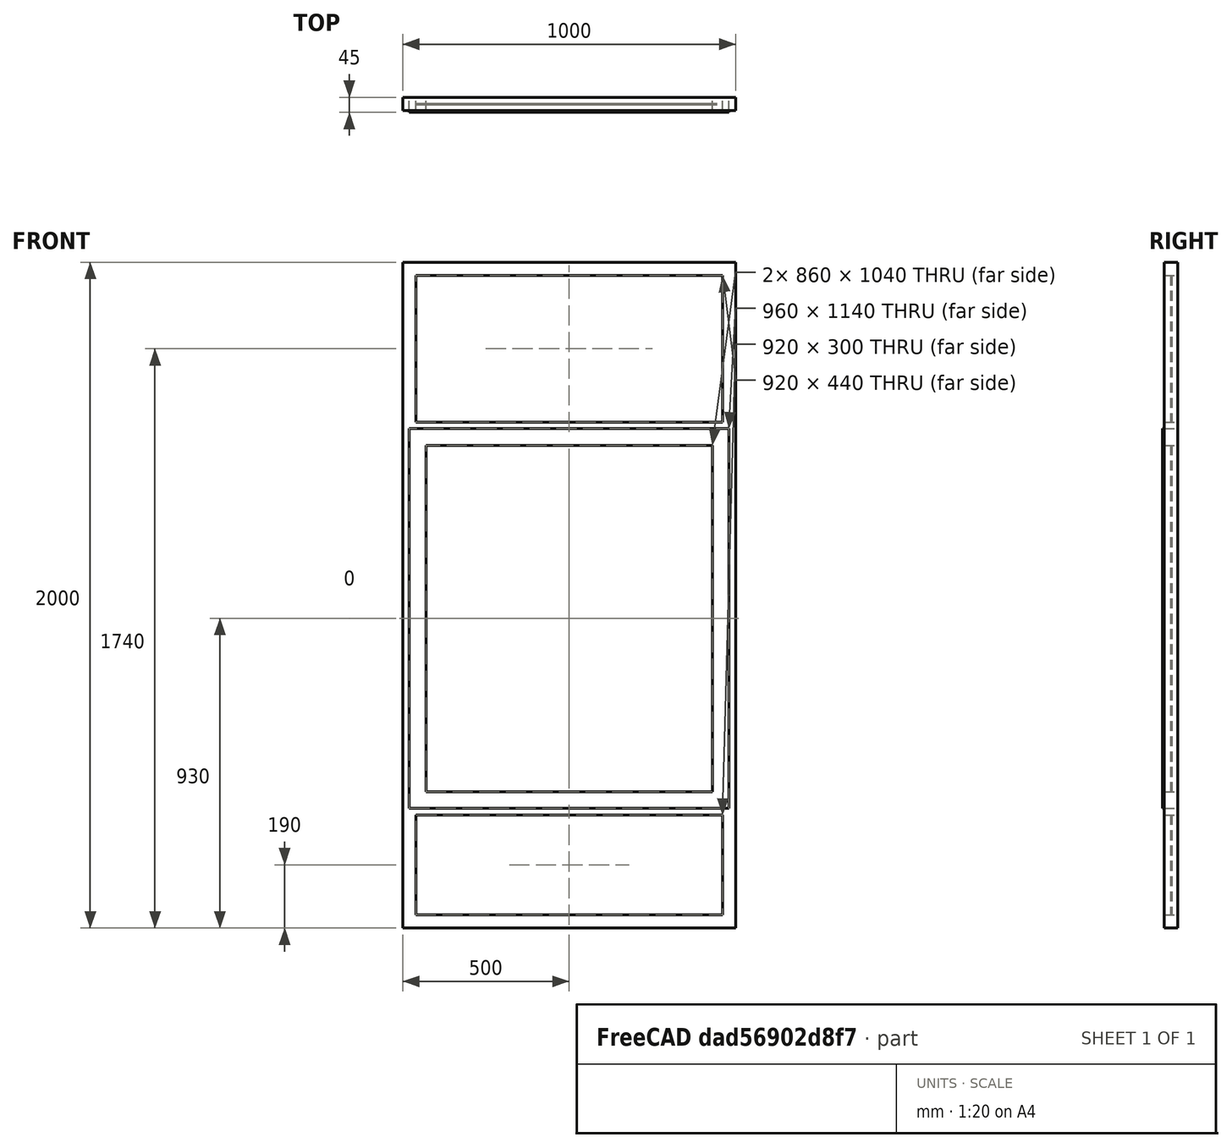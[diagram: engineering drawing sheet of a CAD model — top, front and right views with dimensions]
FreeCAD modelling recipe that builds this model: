
FCSTD DOCUMENT  (FreeCAD 0.16R6704 (Git))
Label: Maxim Air with fixed glass
License: CreativeCommons Attribution
LicenseURL: http://creativecommons.org/licenses/by/4.0/
objects: Sketcher::SketchObject×2, Part::FeaturePython×1, App::DocumentObjectGroup×1
note: 3 computed .brp shape members not serialized (recipe doc carries the construction recipe); baked Part::Feature solids carry a one-line shape summary decoded from their .brp

FEATURE [Sketcher::SketchObject] Sketch187
  Placement = pos=(0,0,0) rot=(1,0,0;1.5708rad)
  sketch-geometry (24):
    g0: LineSegment StartX=1000 StartY=2000 StartZ=0 EndX=0 EndY=2000 EndZ=0
    g1: LineSegment StartX=0 StartY=2000 StartZ=0 EndX=0 EndY=0 EndZ=0
    g2: LineSegment StartX=0 StartY=0 StartZ=0 EndX=1000 EndY=0 EndZ=0
    g3: LineSegment StartX=1000 StartY=0 StartZ=0 EndX=1000 EndY=2000 EndZ=0
    g4: LineSegment StartX=40 StartY=340 StartZ=0 EndX=960 EndY=340 EndZ=0
    g5: LineSegment StartX=960 StartY=340 StartZ=0 EndX=960 EndY=40 EndZ=0
    g6: LineSegment StartX=960 StartY=40 StartZ=0 EndX=40 EndY=40 EndZ=0
    g7: LineSegment StartX=40 StartY=40 StartZ=0 EndX=40 EndY=340 EndZ=0
    g8: LineSegment StartX=40 StartY=1960 StartZ=0 EndX=960 EndY=1960 EndZ=0
    g9: LineSegment StartX=960 StartY=1960 StartZ=0 EndX=960 EndY=1520 EndZ=0
    g10: LineSegment StartX=960 StartY=1520 StartZ=0 EndX=40 EndY=1520 EndZ=0
    g11: LineSegment StartX=40 StartY=1520 StartZ=0 EndX=40 EndY=1960 EndZ=0
    g12: LineSegment StartX=20 StartY=1500 StartZ=0 EndX=980 EndY=1500 EndZ=0
    g13: LineSegment StartX=980 StartY=1500 StartZ=0 EndX=980 EndY=360 EndZ=0
    g14: LineSegment StartX=980 StartY=360 StartZ=0 EndX=20 EndY=360 EndZ=0
    g15: LineSegment StartX=20 StartY=360 StartZ=0 EndX=20 EndY=1500 EndZ=0
    g16: LineSegment StartX=70 StartY=1450 StartZ=0 EndX=930 EndY=1450 EndZ=0
    g17: LineSegment StartX=930 StartY=1450 StartZ=0 EndX=930 EndY=410 EndZ=0
    g18: LineSegment StartX=930 StartY=410 StartZ=0 EndX=70 EndY=410 EndZ=0
    g19: LineSegment StartX=70 StartY=410 StartZ=0 EndX=70 EndY=1450 EndZ=0
    g20: LineSegment StartX=40 StartY=380 StartZ=0 EndX=960 EndY=380 EndZ=0
    g21: LineSegment StartX=960 StartY=380 StartZ=0 EndX=960 EndY=1480 EndZ=0
    g22: LineSegment StartX=960 StartY=1480 StartZ=0 EndX=40 EndY=1480 EndZ=0
    g23: LineSegment StartX=40 StartY=1480 StartZ=0 EndX=40 EndY=380 EndZ=0
  constraints (71):
    c: Coincident(g0,g1)
    c: Horizontal(g0)
    c: Coincident(g1,g2)
    c: Vertical(g1)
    c: Coincident(g2,g3)
    c: Horizontal(g2)
    c: Coincident(g3,g0)
    c: Coincident(g4,g5)
    c: Horizontal(g4)
    c: Coincident(g5,g6)
    c: Vertical(g5)
    c: Coincident(g6,g7)
    c: Horizontal(g6)
    c: Coincident(g7,g4)
    c: Coincident(g8,g9)
    c: Horizontal(g8)
    c: Coincident(g9,g10)
    c: Vertical(g9)
    c: Coincident(g10,g11)
    c: Horizontal(g10)
    c: Coincident(g11,g8)
    c: Coincident(g12,g13)
    c: Horizontal(g12)
    c: Coincident(g13,g14)
    c: Vertical(g13)
    c: Coincident(g14,g15)
    c: Horizontal(g14)
    c: Coincident(g15,g12)
    c: Coincident(g16,g17)
    c: Horizontal(g16)
    c: Coincident(g17,g18)
    c: Vertical(g17)
    c: Coincident(g18,g19)
    c: Horizontal(g18)
    c: Coincident(g19,g16)
    c: Coincident(g20,g21)
    c: Horizontal(g20)
    c: Coincident(g21,g22)
    c: Vertical(g21)
    c: Coincident(g22,g23)
    c: Horizontal(g22)
    c: Coincident(g23,g20)
    c: DistanceX(g-1,g2) = 1000  'Largura do vão'
    c: DistanceY(g-1,g0) = 2000  'Altura do vão'
    c: Coincident(g1,g-1)
    c: DistanceX(g-1,g6) = 40  'Largura perfil vertical 1'
    c: DistanceY(g-1,g6) = 40  'Altura perfil inferior'
    c: DistanceY(g6,g4) = 300  'Altura vidro inferior'
    c: DistanceX(g20,g4) = 0  'Constraint49'
    c: DistanceX(g20,g4) = 0
    c: DistanceX(g10,g22) = 0
    c: DistanceX(g9,g21) = 0
    c: DistanceY(g8,g0) = 40  'Altura perfil superior'
    c: DistanceX(g5,g2) = 40  'Largura perfil vertical 2'
    c: DistanceY(g22,g10) = 40  'Altura perfil bandeira'
    c: DistanceY(g4,g20) = 40  'Altura montantel inferior maximar'
    c: DistanceX(g22,g16) = 30  'Largura perfil vertical 1 maximar'
    c: DistanceY(g16,g22) = 30  'Aaltura perfil superior maximar'
    c: DistanceX(g16,g21) = 30  'Largura perfil vertical 2 maximar'
    c: Vertical(g11)
    c: Vertical(g23)
    c: DistanceY(g20,g18) = 30  'Altura perfil inferior maximar'
    c: DistanceY(g22,g12) = 20  'Altura arremate superior'
    c: DistanceX(g12,g22) = 20  'Largura arremate vertical 1'
    c: DistanceX(g21,g12) = 20  'Largura arremate vertical 2'
    c: DistanceY(g14,g20) = 20  'Altura arremate inferior'
    c: Vertical(g7)
    c: Vertical(g19)
    c: Vertical(g15)
    c: DistanceY(g20,g22) = 1100  'Altura maximar'
    c: Vertical(g3)
FEATURE [Part::FeaturePython] Window118  label="Maxim Air with fixed glass "  # WARN: FeaturePython — macro-defined, semantics opaque (R4)
  Base = -> Sketch187
  Height = 0
  HoleDepth = 0
  MoveWithHost = true
  Normal = (0,1,0)
  Preset = 0
  Role = 0
  Width = 0
  WindowParts = CAIXILHO | Frame | Wire0,Wire1,Wire2,Wire3 | 40.0 | 0.0 | JANELA | Frame | Wire3,Wire4 | 40.0 | 0.0 | ARREMATE | Frame | Wire4,Wire3 | 5.0 | -5.0 | VIDRO SUPERIOR | Glass panel | Wire2 | 4.0 | 18.0 | VIDRO MAXIMAR | Glass panel | Wire4 | 4.0 | 18.0 | VIDRO INFERIOR | Glass panel | Wire1 | 4.0 | 18.0
FEATURE [Sketcher::SketchObject] Sketch188  label="Opening indication "
  ExternalGeometry = -> [Window118]
  Placement = pos=(0,18,0) rot=(1,0,0;1.5708rad)
  Support = -> Window118 [Face49]
  sketch-geometry (3):
    g0: LineSegment [constr] StartX=500 StartY=2100 StartZ=0 EndX=500 EndY=-239.743 EndZ=0
    g1: LineSegment StartX=70 StartY=1450 StartZ=0 EndX=500 EndY=410 EndZ=0
    g2: LineSegment StartX=500 StartY=410 StartZ=0 EndX=930 EndY=1450 EndZ=0
  constraints (7):
    c: Vertical(g0)
    c: Symmetric(g-4,g-5,g0)
    c: Coincident(g-4,g1)
    c: PointOnObject(g1,g-6)
    c: Coincident(g1,g2)
    c: Coincident(g2,g-5)
    c: PointOnObject(g1,g0)
FEATURE [App::DocumentObjectGroup] Grupo088  label="Maxim Air with fixed glass"
  Group = -> [Window118,Sketch188]
